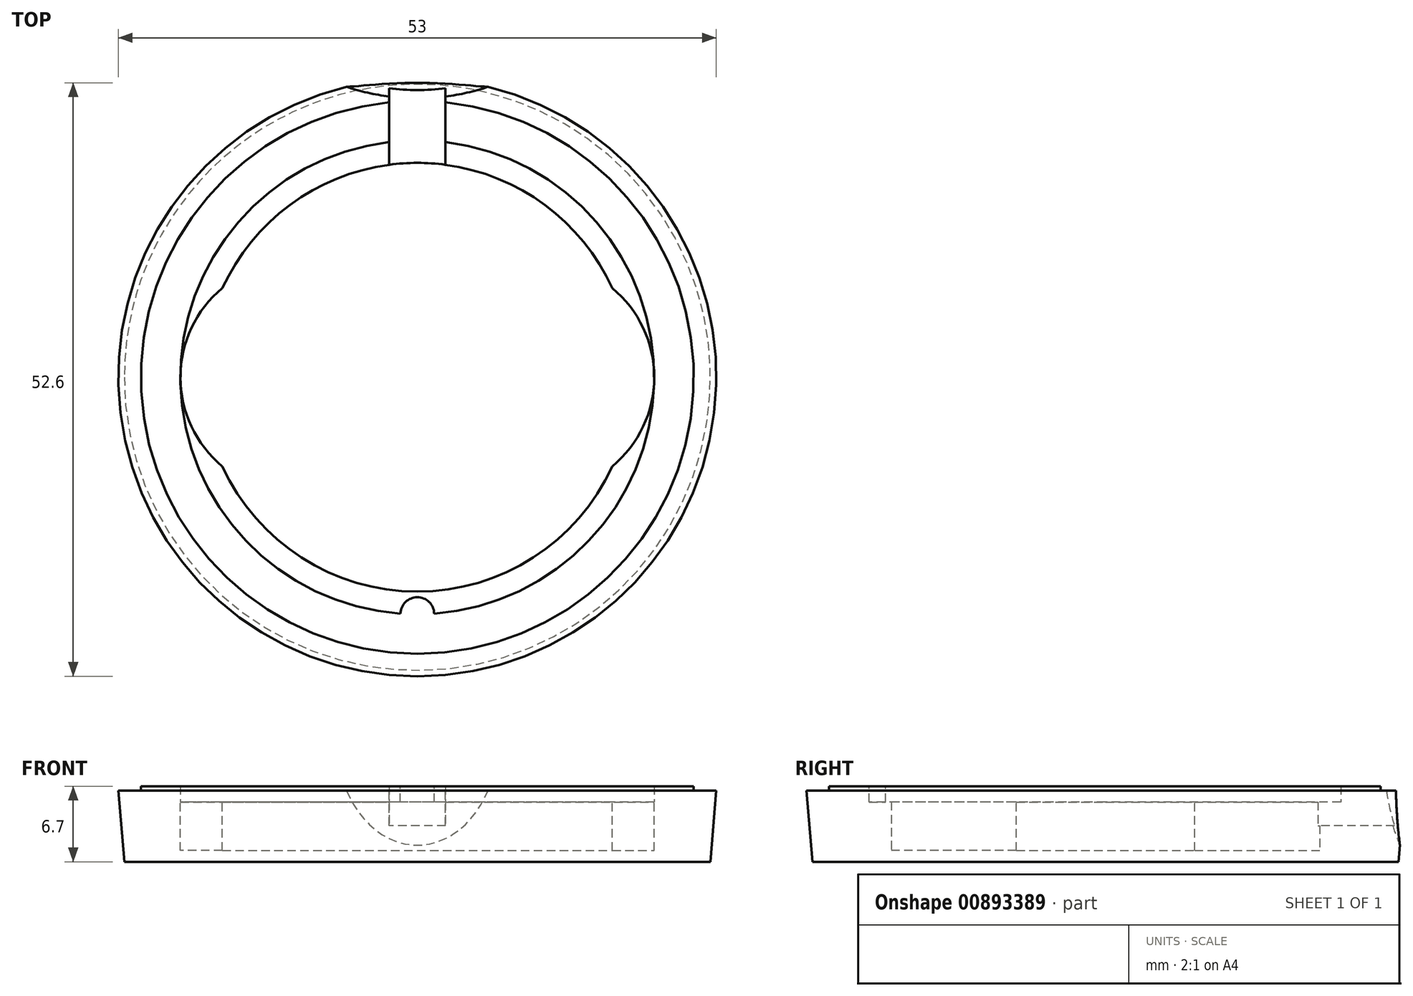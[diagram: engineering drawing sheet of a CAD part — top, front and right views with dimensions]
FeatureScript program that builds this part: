
annotation { "Feature Type Name" : "Feature", "Feature Type Description" : "" }
export const myFeature = defineFeature(function(context is Context, id is Id, definition is map)
    precondition{}
    {
        {
            var Q0;
            Q0=qCreatedBy(makeId("Front.planeOp"),FACE);
            var sketch = newSketch(context, id + "F0", { "sketchPlane" : qUnion([Q0])});
            skLineSegment(sketch, "E0", {"start": v(0, 0) * mm, "end": v(0, 1) * mm});
            skLineSegment(sketch, "E1", {"start": v(-21, 6.7) * mm, "end": v(-24.5, 6.7) * mm});
            skLineSegment(sketch, "E2", {"start": v(-24.5, 6.7) * mm, "end": v(-24.5, 6.3) * mm});
            skLineSegment(sketch, "E3", {"start": v(-24.5, 6.3) * mm, "end": v(-26.5, 6.3) * mm});
            skLineSegment(sketch, "E4", {"start": v(-26.5, 6.3) * mm, "end": v(-25.97, 0) * mm});
            skLineSegment(sketch, "E5", {"start": v(0, 0) * mm, "end": v(-25.97, 0) * mm});
            skLineSegment(sketch, "E6", {"start": v(-21, 6.7) * mm, "end": v(-21, 5.3) * mm});
            skLineSegment(sketch, "E7", {"start": v(-21, 5.3) * mm, "end": v(-19, 5.3) * mm});
            skLineSegment(sketch, "E8", {"start": v(-19, 5.3) * mm, "end": v(-19, 1) * mm});
            skLineSegment(sketch, "E9", {"start": v(-19, 1) * mm, "end": v(0, 1) * mm});
            skSolve(sketch);
        }
        {
            var Q0;
            Q0=makeQuery(id+"F0.imprint","IMPRINT",FACE,{"disambiguationData":[TD([[makeQuery(id+"F0.imprint","IMPRINT",EDGE,{"derivedFrom":sQuery(id+"F0.wireOp",EDGE,"E0")}),1.0]])]});
            var Q1;
            Q1=sQuery(id+"F0.wireOp",EDGE,"E0");
            revolve(context, id + "F1", {"surfaceOperationType" : NewSurfaceOperationType.NEW, "entities" : qUnion([Q0]), "axis" : qUnion([Q1]), "revolveType" : RevolveType.FULL});
        }
        {
            var Q0;
            Q0=makeQuery(id+"F1.opRevolve","SWEPT_FACE",FACE,{"disambiguationData":[OSD([sQuery(id+"F0.wireOp",EDGE,"E7")])]});
            var sketch = newSketch(context, id + "F2", { "sketchPlane" : qUnion([Q0])});
            skCircle(sketch, "E10", {"center": v(-10.75, 0) * mm, "radius": 10.25 * mm});
            skCircle(sketch, "E11", {"center": v(10.75, 0) * mm, "radius": 10.25 * mm});
            skSolve(sketch);
        }
        {
            var Q0;
            {var subQ0=sQuery(id+"F2.wireOp",EDGE,"E10");var subQ1=sQuery(id+"F0.wireOp",EDGE,"E7");var subQ2=makeQuery(id+"F2.imprint","INTERSECT",VERTEX,{"derivedFrom":[makeQuery(id+"F1.opRevolve","SWEPT_EDGE",EDGE,{"disambiguationData":[OSD([sQuery(id+"F0.wireOp",EDGE,"E6"),subQ1])]}),subQ0]});Q0=makeQuery(id+"F2.imprint","IMPRINT",FACE,{"disambiguationData":[TD([[makeQuery(id+"F2.imprint","IMPRINT",EDGE,{"disambiguationData":[TD([[subQ2,1.0]])],"derivedFrom":subQ0}),1.0]])]});}
            var Q1;
            {var subQ0=sQuery(id+"F2.wireOp",EDGE,"E10");var subQ1=makeQuery(id+"F1.opRevolve","SWEPT_EDGE",EDGE,{"disambiguationData":[OSD([sQuery(id+"F0.wireOp",EDGE,"E7"),sQuery(id+"F0.wireOp",EDGE,"E8")])]});var subQ2=makeQuery(id+"F2.imprint","INTERSECT",VERTEX,{"disambiguationData":[OD(0.0)],"derivedFrom":[subQ1,subQ0]});Q1=makeQuery(id+"F2.imprint","IMPRINT",FACE,{"disambiguationData":[TD([[makeQuery(id+"F2.imprint","IMPRINT",EDGE,{"disambiguationData":[TD([[subQ2,1.0]])],"derivedFrom":subQ0}),1.0]])]});}
            var Q2;
            {var subQ0=sQuery(id+"F2.wireOp",EDGE,"E11");var subQ1=makeQuery(id+"F1.opRevolve","SWEPT_EDGE",EDGE,{"disambiguationData":[OSD([sQuery(id+"F0.wireOp",EDGE,"E7"),sQuery(id+"F0.wireOp",EDGE,"E8")])]});var subQ2=makeQuery(id+"F2.imprint","INTERSECT",VERTEX,{"disambiguationData":[OD(0.0)],"derivedFrom":[subQ1,subQ0]});Q2=makeQuery(id+"F2.imprint","IMPRINT",FACE,{"disambiguationData":[TD([[makeQuery(id+"F2.imprint","IMPRINT",EDGE,{"disambiguationData":[TD([[subQ2,-1.0]])],"derivedFrom":subQ0}),1.0]])]});}
            var Q3;
            {var subQ0=sQuery(id+"F2.wireOp",EDGE,"E11");var subQ1=sQuery(id+"F0.wireOp",EDGE,"E7");var subQ2=makeQuery(id+"F2.imprint","INTERSECT",VERTEX,{"derivedFrom":[makeQuery(id+"F1.opRevolve","SWEPT_EDGE",EDGE,{"disambiguationData":[OSD([sQuery(id+"F0.wireOp",EDGE,"E6"),subQ1])]}),subQ0]});Q3=makeQuery(id+"F2.imprint","IMPRINT",FACE,{"disambiguationData":[TD([[makeQuery(id+"F2.imprint","IMPRINT",EDGE,{"disambiguationData":[TD([[subQ2,-1.0]])],"derivedFrom":subQ0}),1.0]])]});}
            var Q4;
            Q4=makeQuery(id+"F1.opRevolve","SWEPT_FACE",FACE,{"disambiguationData":[OSD([sQuery(id+"F0.wireOp",EDGE,"E9")])]});
            extrude(context, id + "F3", {"entities" : qUnion([Q0, Q1, Q2, Q3]), "operationType" : NewBodyOperationType.REMOVE, "endBound" : BoundingType.UP_TO_SURFACE, "oppositeDirection" : true, "depth" : 25 * mm, "endBoundEntityFace" : qUnion([Q4]), "offsetDistance" : 25 * mm});
        }
        {
            var Q0;
            Q0=makeQuery(id+"F1.opRevolve","SWEPT_FACE",FACE,{"disambiguationData":[OSD([sQuery(id+"F0.wireOp",EDGE,"E1")])]});
            var sketch = newSketch(context, id + "F4", { "sketchPlane" : qUnion([Q0])});
            skCircle(sketch, "E12", {"center": v(0, -21) * mm, "radius": 1.5 * mm});
            skSolve(sketch);
        }
        {
            var Q0;
            Q0 = qSketchRegion(id + "F4", true);
            extrude(context, id + "F5", {"entities" : qUnion([Q0]), "operationType" : NewBodyOperationType.ADD, "endBound" : BoundingType.UP_TO_NEXT, "oppositeDirection" : true, "depth" : 25 * mm, "offsetDistance" : 25 * mm});
        }
        {
            var Q0;
            Q0=qCreatedBy(makeId("Right.planeOp"),FACE);
            var sketch = newSketch(context, id + "F6", { "sketchPlane" : qUnion([Q0])});
            skArc(sketch, "E13", {"start": v(44.5, 29.3) * mm, "mid": v(24.5, 9.3) * mm, "end": v(44.5, -10.7) * mm});
            skLineSegment(sketch, "E14", {"start": v(44.5, -37.13) * mm, "end": v(44.5, 66.92) * mm, "construction": true});
            skLineSegment(sketch, "E15", {"start": v(44.5, 29.3) * mm, "end": v(44.5, -10.7) * mm});
            skLineSegment(sketch, "E16", {"start": v(26.5, 6.3) * mm, "end": v(25.97, 0) * mm, "construction": true});
            skLineSegment(sketch, "E17", {"start": v(26.5, 6.3) * mm, "end": v(26.5, 7.55) * mm, "construction": true});
            skLineSegment(sketch, "E18.0.0", {"start": v(-26.5, 6.3) * mm, "end": v(26.5, 6.3) * mm, "construction": true});
            skSolve(sketch);
        }
        {
            var Q0;
            Q0=makeQuery(id+"F6.imprint","IMPRINT",FACE,{"disambiguationData":[TD([[makeQuery(id+"F6.imprint","IMPRINT",EDGE,{"derivedFrom":sQuery(id+"F6.wireOp",EDGE,"E13")}),1.0]])]});
            var Q1;
            Q1=sQuery(id+"F6.wireOp",EDGE,"E14");
            revolve(context, id + "F7", {"operationType" : NewBodyOperationType.REMOVE, "surfaceOperationType" : NewSurfaceOperationType.NEW, "entities" : qUnion([Q0]), "axis" : qUnion([Q1]), "revolveType" : RevolveType.FULL, "oppositeDirection" : true});
        }
        {
            var Q0;
            Q0=qCreatedBy(makeId("Front.planeOp"),FACE);
            var sketch = newSketch(context, id + "F8", { "sketchPlane" : qUnion([Q0])});
            skLineSegment(sketch, "E19.bottom", {"start": v(2.5, 8.89) * mm, "end": v(-2.5, 8.89) * mm});
            skLineSegment(sketch, "E19.top", {"start": v(2.5, 3.2) * mm, "end": v(-2.5, 3.2) * mm});
            skLineSegment(sketch, "E19.left", {"start": v(2.5, 8.89) * mm, "end": v(2.5, 3.2) * mm});
            skLineSegment(sketch, "E19.right", {"start": v(-2.5, 8.89) * mm, "end": v(-2.5, 3.2) * mm});
            skPoint(sketch, "E19.middle", {"position": v(0, 6.04) * mm});
            skSolve(sketch);
        }
        {
            var Q0;
            Q0=makeQuery(id+"F8.imprint","IMPRINT",FACE,{"disambiguationData":[TD([[makeQuery(id+"F8.imprint","IMPRINT",EDGE,{"derivedFrom":sQuery(id+"F8.wireOp",EDGE,"E19.bottom")}),1.0]])]});
            extrude(context, id + "F9", {"entities" : qUnion([Q0]), "operationType" : NewBodyOperationType.REMOVE, "endBound" : BoundingType.THROUGH_ALL, "oppositeDirection" : true, "depth" : 25 * mm, "offsetDistance" : 25 * mm});
        }
    });
